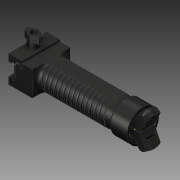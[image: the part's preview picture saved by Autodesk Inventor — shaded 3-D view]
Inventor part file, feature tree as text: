
AUTODESK INVENTOR PART (.ipt)
format: ipt  version: 2017 (Build 210142000, 142)  size: 1,163,776 bytes
history: native  units: in
note: dims shown in document units (in); Inventor stores cm internally (conversion verified against a paired STEP export)
features: sketch x24, extrude x21, other x7, plane x5, move_body x4, revolve x2, fillet x1, shell x1, split x1, mirror x1
ambient origin geometry x8: Origin, YZ Plane, XZ Plane, XY Plane, X Axis, Y Axis, Z Axis, Center Point
bodies: Body1 (feature_tree), Body2 (feature_tree), Body3 (feature_tree), Body4 (feature_tree), Body5 (feature_tree), Body6 (feature_tree), Body7 (feature_tree), Body8 (feature_tree), Body9 (feature_tree), Body10 (feature_tree), Body11 (feature_tree), Body12 (feature_tree), Body13 (feature_tree), Body14 (feature_tree), Body15 (feature_tree), Body16 (feature_tree)
feature tree (67):
  other  "Grip"
  sketch  "Sketch1"  dims[d9=0.9487in d141=0.1in]
  revolve  "Revolution2"  [1 undecoded]
  extrude  "Body Cutout 1"  Depth=0.1in
  extrude  "Body Cutout 2"  Depth=0.1in
  extrude  "Rail Mount Cutout"  Depth=0.1in
  plane  "Work Plane3"
  extrude  "Rail Mount Tab 1"  Depth=0.1in
  plane  "Work Plane4"
  extrude  "Rail Mount Tab 2"  Depth=0.1in
  extrude  "Screw Relief Cut"  Depth=0.1in
  extrude  "Nut"  Depth=0.01in
  extrude  "Outside Cut"  Depth=0.01in
  plane  "Work Plane5"
  extrude  "Locking Plate Body"  Depth=0.01in
  extrude  "Locking Plate Thru Hole"  TaperAngle=90.0deg  [1 undecoded]
  extrude  "Wing Nut Body"  Depth=3.75in TaperAngle=0.0deg
  extrude  "Wing Nut Grip"  Depth=1.35in TaperAngle=0.0deg
  fillet  "Fillet1"  Radius=0.292in
  extrude  "screw Head"  [1 undecoded]
  extrude  "Screw Threads"  [1 undecoded]
  shell  "Shell1"  Thickness=0.1925in
  plane  "Work Plane6"
  revolve  "Revolution3"  [1 undecoded]
  split  "Split1"
  extrude  "BPL Body"  Depth=0.4115in
  plane  "Work Plane9"
  extrude  "BPL Left Cutout"  Depth=0.05in
  extrude  "BPL Foot"  TaperAngle=0.0deg  [1 undecoded]
  extrude  "BPL Thru Holes"  Depth=0.348in TaperAngle=0.0deg
  extrude  "BPL Upper Body Cut 1"  Depth=0.0835in
  extrude  "BPL Lower Body Cut"  Depth=0.05in
  extrude  "BPL Angle"  Depth=0.384in TaperAngle=0.0deg
  sketch  "Sketch33"  dims[d275=0.1in d277=0.1175in d278=0.0in d279=1.8in d280=0.0in d282=0.1in d299=0.4383in d306=0.3785in d307=0.5in d308=0.2in d310=90.0deg d312=0.8in d313=0.0in d314=0.0in d315=0.5in d316=0.0in d317=0.715in d318=0.0in d319=0.0815in d332=1.0749in d336=0.33in d337=0.0815in d338=0.0815in d339=0.0815in d340=0.0815in d341=0.0815in d342=0.0815in d343=0.0815in d344=0.0815in d345=0.715in d346=0.0in d347=0.35in d348=0.0in d349=0.35in d350=0.0in d351=0.715in d352=0.0in d353=0.0in d354=0.035in d355=0.0in d356=-4.05in d357=0.0in d358=0.0in d359=4.0in d360=0.0in d361=0.0in d362=-4.0in d363=0.0in d364=0.0in]
  move_body  "Move Body1"
  mirror  "Mirror1"
  move_body  "Move Body2"
  move_body  "Move Body3"
  move_body  "Move Body4"
  sketch  "Sketch6"  dims[d147=0.1in d150=0.1in]
  sketch  "Sketch8"  dims[d153=0.1in d156=0.1in]
  sketch  "Sketch9"  dims[d159=0.1in d162=0.1in]
  sketch  "Sketch10"  dims[d165=0.1in d168=0.1in]
  sketch  "Sketch12"  dims[d171=0.1in d174=0.1in]
  sketch  "Sketch13"  dims[d177=0.1in d180=0.1in]
  sketch  "Sketch14"  dims[d187=0.19in d188=0.01in]
  sketch  "Sketch15"  dims[d189=0.01in d190=0.01in]
  sketch  "Sketch16"  dims[d191=0.01in d192=0.01in]
  other  "Locking Plate"
  sketch  "Sketch17"  dims[d206=0.075in d207=90.0deg]
  sketch  "Sketch18"  dims[d210=0.615in d211=3.75in d212=0.0in]
  other  "Wing Nut"
  sketch  "Sketch19"  dims[d213=0.0in d215=1.35in d216=0.0in d226=0.292in]
  sketch  "Sketch20"  dims[d228=1.87in d229=0.0in d230=-0.0395in]
  other  "Screw"
  sketch  "Sketch21"  dims[d233=0.1925in d234=0.0in d238=-0.0395in d239=0.1925in d240=0.0in]
  sketch  "Sketch23"  dims[d242=0.099in d243=1.11in d244=0.0in]
  other  "Bi-pod Left"
  sketch  "Sketch24"  dims[d246=0.136in d247=0.0in d248=0.4115in]
  sketch  "Sketch26"  dims[d249=0.324in d253=0.05in]
  sketch  "Sketch27"  dims[d254=0.2125in d255=0.0in d256=0.0in]
  sketch  "Sketch28"  dims[d260=1.858in d261=0.0in d262=0.348in d263=0.0in]
  sketch  "Sketch29"  dims[d264=0.2405in d265=0.0835in]
  sketch  "Sketch30"  dims[d266=0.2in d267=0.0in d271=0.05in]
  sketch  "Sketch31"  dims[d272=0.1425in d273=0.384in d274=0.0in]
  other  "Pattern of Bi-pod Left:1"
  other  "Bi-pod Right"
note: 6 required parameter values undecoded (feature->parameter linkage not recoverable at this tier; creation-order binding heuristic only, values carry confidence <= 0.55)